# Revit family: Sanitary_Showers_hansgrohe_24311AUS-Pulsify-Shower-set-105-1jet-wit_1
name_source: partatom
category: Plumbing Fixtures
revit_build: Autodesk Revit 2018 (Build: 20170223_1515(x64)
units: mm (PartAtom-declared; Revit-internal decimal feet)

## family parameters
Always vertical = No
Cut with Voids When Loaded = No
OmniClass Number = 23.31.17.00
Part Type = Normal
Room Calculation Point = No
Round Connector Dimension = Use Diameter
Shared = No
Work Plane-Based = Yes

## types (3) — shared parameters
Always visible = Yes
BIMobject category = Showers
Default Elevation = 1219.2 mm  [stored 4 ft]
Design country = Germany
EAN code = 4059625380345
Edition number = 1
GTIN code = https://4059625380345
IFC Classification = Sanitary Terminal
Installation instructions = https://www.hansgrohe.com
Manufacturer country = Germany
Manufacturer name = hansgrohe
Material 3 = Hansgrohe - Metal - Graphite
Material main = Metal
Material secondary = Chrome
OmniClass Code = 23-31 17 00
OmniClass Description = Showers
Product Guid = ab0366b8-fec5-4197-878a-95091888d487
Product SKU = 24311AUS
Product data url = https://www.bimobject.com
Product family = Pulsify
Product group = Wallbar sets
Product name = 24311AUS Pulsify Shower set 105 1jet with shower bar 65 cm
Product url = https://www.hansgrohe.com
QR code = https://www.bimobject.com
Technical description = https://www.hansgrohe.com
UNSPSC Code = 30181503
Uniclass 1.4 Code = L7214
Uniclass 1.4 Description = Showers
Weight Net (Kg) = 1.1

## per-type parameters (varying)
| type | Material 1 |
| 003 Chrome | Hansgrohe - Metal - 003 Chrome |
| 673 Matte Black | Hansgrohe - Metal - 673 Matte Black |
| 703 Matt White | Hansgrohe - Metal - 703 Matt White |

note: [stored X ft] marks values corroborated as IEEE doubles in the binary element streams (Revit-internal decimal feet)

## geometry (parser evidence)
native form markers: Sweep x3
no freeform markers — native parametric forms only
